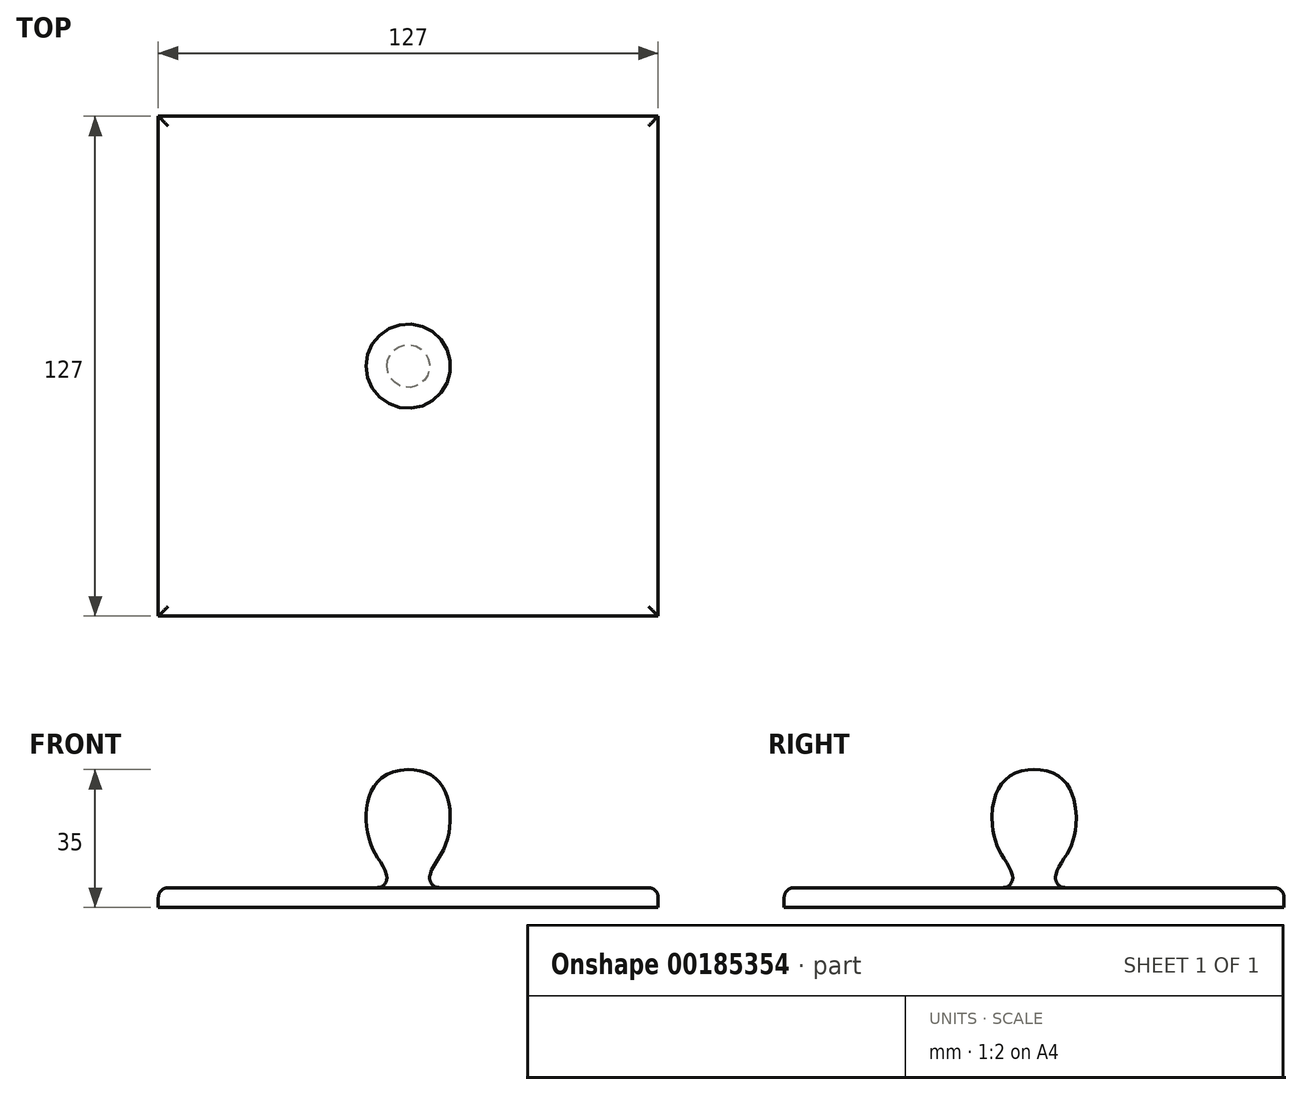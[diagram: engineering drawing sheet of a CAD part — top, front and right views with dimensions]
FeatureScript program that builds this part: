
annotation { "Feature Type Name" : "Feature", "Feature Type Description" : "" }
export const myFeature = defineFeature(function(context is Context, id is Id, definition is map)
    precondition{}
    {
        {
            assignVariable(context, id + "F0", {"name" : "StampThickness", "anyValue" : 5});
        }
        {
            var Q0;
            Q0=qCreatedBy(makeId("Top.planeOp"),FACE);
            var sketch = newSketch(context, id + "F1", { "sketchPlane" : qUnion([Q0])});
            skLineSegment(sketch, "E0.bottom", {"start": v(63.5, -63.5) * mm, "end": v(-63.5, -63.5) * mm});
            skLineSegment(sketch, "E0.top", {"start": v(63.5, 63.5) * mm, "end": v(-63.5, 63.5) * mm});
            skLineSegment(sketch, "E0.left", {"start": v(63.5, -63.5) * mm, "end": v(63.5, 63.5) * mm});
            skLineSegment(sketch, "E0.right", {"start": v(-63.5, -63.5) * mm, "end": v(-63.5, 63.5) * mm});
            skPoint(sketch, "E0.middle", {"position": v(0, 0) * mm});
            skSolve(sketch);
        }
        {
            var Q0;
            Q0 = qSketchRegion(id + "F1", true);
            extrude(context, id + "F2", {"entities" : qUnion([Q0]), "depth" : (getVariable(context, 'StampThickness')) * mm, "offsetDistance" : 25 * mm});
        }
        {
            var Q0;
            Q0=qCreatedBy(makeId("Front.planeOp"),FACE);
            var sketch = newSketch(context, id + "F3", { "sketchPlane" : qUnion([Q0])});
            skPoint(sketch, "E1.0", {"position": v(0, 5) * mm});
            skLineSegment(sketch, "E2", {"start": v(0, 5) * mm, "end": v(0, 35) * mm});
            skFitSpline(sketch, "E3", {"points": [v(0, 35) * mm, v(-10.2, 27.02) * mm, v(-8.85, 14.46) * mm, v(-5.33, 5) * mm], "startDerivative": vector(-56, -0.98) * mm, "endDerivative": vector(-4.85, -43.21) * mm});
            skLineSegment(sketch, "E4", {"start": v(-5.33, 5) * mm, "end": v(0, 5) * mm});
            skSolve(sketch);
        }
        {
            var Q0;
            Q0 = qSketchRegion(id + "F3", true);
            var Q1;
            Q1=sQuery(id+"F3.wireOp",EDGE,"E2");
            revolve(context, id + "F4", {"operationType" : NewBodyOperationType.ADD, "surfaceOperationType" : NewSurfaceOperationType.NEW, "entities" : qUnion([Q0]), "axis" : qUnion([Q1]), "revolveType" : RevolveType.FULL});
        }
        {
            var Q0;
            Q0=makeQuery(id+"F2.opExtrude","CAP_FACE",FACE,{"disambiguationData":[OSD([sQuery(id+"F1.wireOp",EDGE,"E0.bottom"),sQuery(id+"F1.wireOp",EDGE,"E0.top"),sQuery(id+"F1.wireOp",EDGE,"E0.left"),sQuery(id+"F1.wireOp",EDGE,"E0.right")])],"isStart":false});
            fillet(context, id + "F5", {"entities" : qUnion([Q0]), "radius" : 2.5 * mm, "tangentPropagation" : true, "allowEdgeOverflow" : false});
        }
    });
